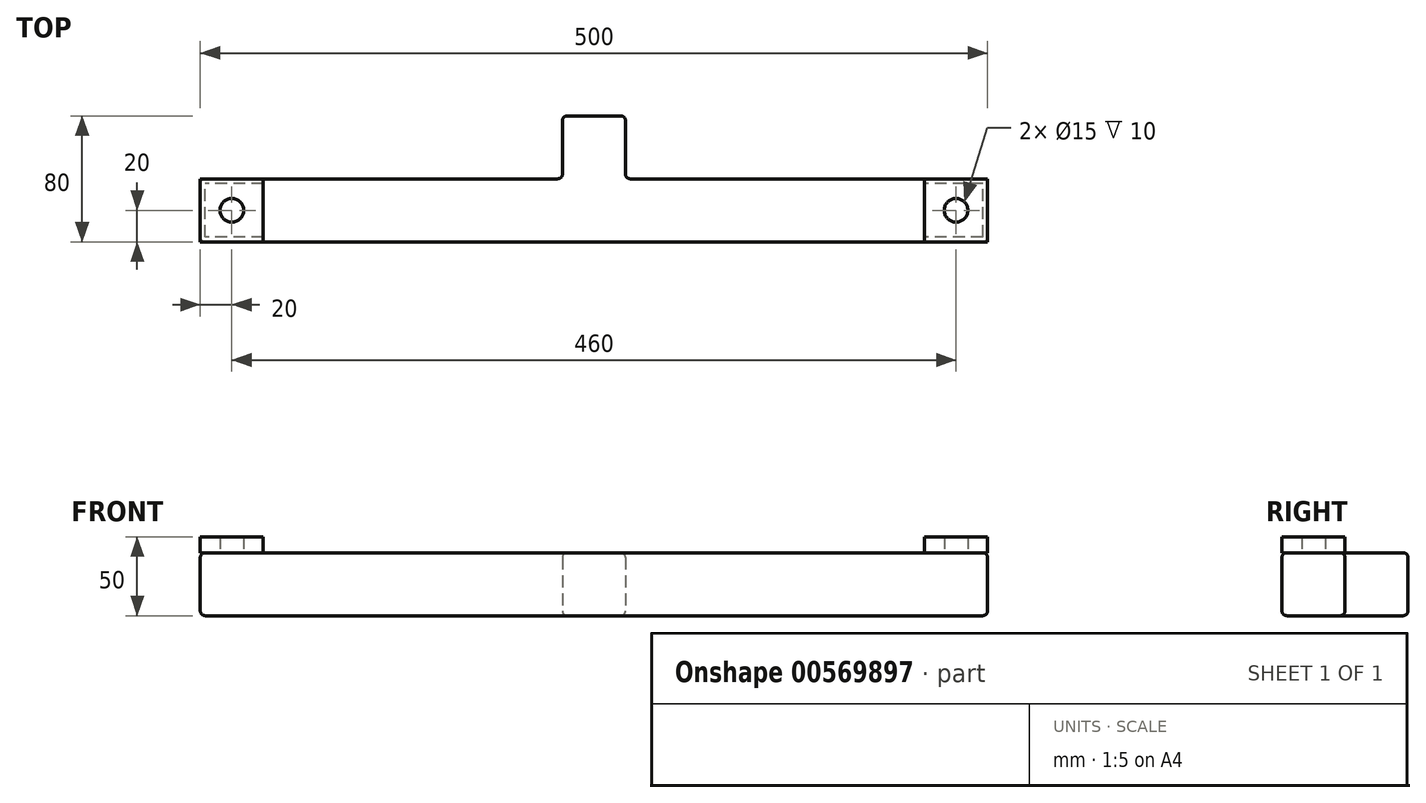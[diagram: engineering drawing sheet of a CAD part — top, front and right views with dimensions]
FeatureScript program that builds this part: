
annotation { "Feature Type Name" : "Feature", "Feature Type Description" : "" }
export const myFeature = defineFeature(function(context is Context, id is Id, definition is map)
    precondition{}
    {
        {
            var Q0;
            Q0=qCreatedBy(makeId("Top.planeOp"),FACE);
            var sketch = newSketch(context, id + "F0", { "sketchPlane" : qUnion([Q0])});
            skLineSegment(sketch, "E0.bottom", {"start": v(250, -20) * mm, "end": v(-250, -20) * mm});
            skLineSegment(sketch, "E0.top", {"start": v(250, 20) * mm, "end": v(20, 20) * mm});
            skLineSegment(sketch, "E0.left", {"start": v(250, -20) * mm, "end": v(250, 20) * mm});
            skLineSegment(sketch, "E0.right", {"start": v(-250, -20) * mm, "end": v(-250, 20) * mm});
            skPoint(sketch, "E0.middle", {"position": v(0, 0) * mm});
            skLineSegment(sketch, "E1.top", {"start": v(-20, 60) * mm, "end": v(20, 60) * mm});
            skLineSegment(sketch, "E1.left", {"start": v(-20, 20) * mm, "end": v(-20, 60) * mm});
            skLineSegment(sketch, "E1.right", {"start": v(20, 20) * mm, "end": v(20, 60) * mm});
            skLineSegment(sketch, "E2.trimOffspring", {"start": v(-20, 20) * mm, "end": v(-250, 20) * mm});
            skSolve(sketch);
        }
        {
            var Q0;
            Q0 = qSketchRegion(id + "F0", true);
            extrude(context, id + "F1", {"entities" : qUnion([Q0]), "depth" : 40 * mm, "offsetDistance" : 25 * mm});
        }
        {
            var Q0;
            Q0=makeQuery(id+"F1.opExtrude","SWEPT_EDGE",EDGE,{"disambiguationData":[OSD([sQuery(id+"F0.wireOp",EDGE,"E0.top"),sQuery(id+"F0.wireOp",EDGE,"E0.left")])]});
            var Q1;
            Q1=makeQuery(id+"F1.opExtrude","SWEPT_EDGE",EDGE,{"disambiguationData":[OSD([sQuery(id+"F0.wireOp",EDGE,"E0.bottom"),sQuery(id+"F0.wireOp",EDGE,"E0.right")])]});
            var Q2;
            Q2=makeQuery(id+"F1.opExtrude","SWEPT_EDGE",EDGE,{"disambiguationData":[OSD([sQuery(id+"F0.wireOp",EDGE,"E0.bottom"),sQuery(id+"F0.wireOp",EDGE,"E0.left")])]});
            var Q3;
            Q3=makeQuery(id+"F1.opExtrude","CAP_EDGE",EDGE,{"disambiguationData":[OSD([sQuery(id+"F0.wireOp",EDGE,"E0.bottom")])],"isStart":true});
            var Q4;
            Q4=makeQuery(id+"F1.opExtrude","CAP_EDGE",EDGE,{"disambiguationData":[OSD([sQuery(id+"F0.wireOp",EDGE,"E0.bottom")])],"isStart":false});
            var Q5;
            Q5=makeQuery(id+"F1.opExtrude","CAP_EDGE",EDGE,{"disambiguationData":[OSD([sQuery(id+"F0.wireOp",EDGE,"E0.top")])],"isStart":false});
            var Q6;
            Q6=makeQuery(id+"F1.opExtrude","CAP_EDGE",EDGE,{"disambiguationData":[OSD([sQuery(id+"F0.wireOp",EDGE,"E0.left")])],"isStart":true});
            var Q7;
            Q7=makeQuery(id+"F1.opExtrude","CAP_EDGE",EDGE,{"disambiguationData":[OSD([sQuery(id+"F0.wireOp",EDGE,"E0.left")])],"isStart":false});
            var Q8;
            Q8=makeQuery(id+"F1.opExtrude","CAP_EDGE",EDGE,{"disambiguationData":[OSD([sQuery(id+"F0.wireOp",EDGE,"E0.right")])],"isStart":false});
            var Q9;
            Q9=makeQuery(id+"F1.opExtrude","SWEPT_EDGE",EDGE,{"disambiguationData":[OSD([sQuery(id+"F0.wireOp",EDGE,"E0.top"),sQuery(id+"F0.wireOp",EDGE,"E1.right")])]});
            var Q10;
            Q10=makeQuery(id+"F1.opExtrude","SWEPT_EDGE",EDGE,{"disambiguationData":[OSD([sQuery(id+"F0.wireOp",EDGE,"E0.right"),sQuery(id+"F0.wireOp",EDGE,"E2.trimOffspring")])]});
            var Q11;
            Q11=makeQuery(id+"F1.opExtrude","CAP_EDGE",EDGE,{"disambiguationData":[OSD([sQuery(id+"F0.wireOp",EDGE,"E0.top")])],"isStart":true});
            var Q12;
            Q12=makeQuery(id+"F1.opExtrude","CAP_EDGE",EDGE,{"disambiguationData":[OSD([sQuery(id+"F0.wireOp",EDGE,"E0.right")])],"isStart":true});
            var Q13;
            Q13=makeQuery(id+"F1.opExtrude","CAP_EDGE",EDGE,{"disambiguationData":[OSD([sQuery(id+"F0.wireOp",EDGE,"E1.right")])],"isStart":true});
            var Q14;
            Q14=makeQuery(id+"F1.opExtrude","CAP_EDGE",EDGE,{"disambiguationData":[OSD([sQuery(id+"F0.wireOp",EDGE,"E1.left")])],"isStart":false});
            var Q15;
            Q15=makeQuery(id+"F1.opExtrude","CAP_EDGE",EDGE,{"disambiguationData":[OSD([sQuery(id+"F0.wireOp",EDGE,"E2.trimOffspring")])],"isStart":false});
            var Q16;
            Q16=makeQuery(id+"F1.opExtrude","CAP_EDGE",EDGE,{"disambiguationData":[OSD([sQuery(id+"F0.wireOp",EDGE,"E1.right")])],"isStart":false});
            var Q17;
            Q17=makeQuery(id+"F1.opExtrude","SWEPT_EDGE",EDGE,{"disambiguationData":[OSD([sQuery(id+"F0.wireOp",EDGE,"E1.top"),sQuery(id+"F0.wireOp",EDGE,"E1.right")])]});
            var Q18;
            Q18=makeQuery(id+"F1.opExtrude","CAP_EDGE",EDGE,{"disambiguationData":[OSD([sQuery(id+"F0.wireOp",EDGE,"E1.top")])],"isStart":false});
            var Q19;
            Q19=makeQuery(id+"F1.opExtrude","CAP_EDGE",EDGE,{"disambiguationData":[OSD([sQuery(id+"F0.wireOp",EDGE,"E2.trimOffspring")])],"isStart":true});
            var Q20;
            Q20=makeQuery(id+"F1.opExtrude","SWEPT_EDGE",EDGE,{"disambiguationData":[OSD([sQuery(id+"F0.wireOp",EDGE,"E1.left"),sQuery(id+"F0.wireOp",EDGE,"E2.trimOffspring")])]});
            var Q21;
            Q21=makeQuery(id+"F1.opExtrude","SWEPT_EDGE",EDGE,{"disambiguationData":[OSD([sQuery(id+"F0.wireOp",EDGE,"E1.top"),sQuery(id+"F0.wireOp",EDGE,"E1.left")])]});
            var Q22;
            Q22=makeQuery(id+"F1.opExtrude","CAP_EDGE",EDGE,{"disambiguationData":[OSD([sQuery(id+"F0.wireOp",EDGE,"E1.left")])],"isStart":true});
            var Q23;
            Q23=makeQuery(id+"F1.opExtrude","CAP_EDGE",EDGE,{"disambiguationData":[OSD([sQuery(id+"F0.wireOp",EDGE,"E1.top")])],"isStart":true});
            fillet(context, id + "F2", {"entities" : qUnion([Q0, Q1, Q2, Q3, Q4, Q5, Q6, Q7, Q8, Q9, Q10, Q11, Q12, Q13, Q14, Q15, Q16, Q17, Q18, Q19, Q20, Q21, Q22, Q23]), "radius" : 3 * mm, "tangentPropagation" : true, "allowEdgeOverflow" : false});
        }
        {
            var Q0;
            Q0=makeQuery(id+"F1.opExtrude","CAP_FACE",FACE,{"disambiguationData":[OSD([sQuery(id+"F0.wireOp",EDGE,"E0.bottom"),sQuery(id+"F0.wireOp",EDGE,"E0.top"),sQuery(id+"F0.wireOp",EDGE,"E0.left"),sQuery(id+"F0.wireOp",EDGE,"E0.right")])],"isStart":false});
            var sketch = newSketch(context, id + "F3", { "sketchPlane" : qUnion([Q0])});
            skLineSegment(sketch, "E3.bottom", {"start": v(-250, 20) * mm, "end": v(-210, 20) * mm});
            skLineSegment(sketch, "E3.top", {"start": v(-250, -20) * mm, "end": v(-210, -20) * mm});
            skLineSegment(sketch, "E3.left", {"start": v(-250, 20) * mm, "end": v(-250, -20) * mm});
            skLineSegment(sketch, "E3.right", {"start": v(-210, 20) * mm, "end": v(-210, -20) * mm});
            skCircle(sketch, "E4", {"center": v(-230, 0) * mm, "radius": 7.5 * mm});
            skLineSegment(sketch, "E5.MirrorCS", {"start": v(250, 20) * mm, "end": v(210, 20) * mm});
            skLineSegment(sketch, "E6.MirrorCS", {"start": v(250, -20) * mm, "end": v(210, -20) * mm});
            skLineSegment(sketch, "E7.MirrorCS", {"start": v(250, 20) * mm, "end": v(250, -20) * mm});
            skCircle(sketch, "E8.MirrorC", {"center": v(230, 0) * mm, "radius": 7.5 * mm});
            skLineSegment(sketch, "E9.MirrorCS", {"start": v(210, 20) * mm, "end": v(210, -20) * mm});
            skSolve(sketch);
        }
        {
            var Q0;
            Q0 = qSketchRegion(id + "F3", true);
            extrude(context, id + "F4", {"entities" : qUnion([Q0]), "operationType" : NewBodyOperationType.ADD, "depth" : 10 * mm, "offsetDistance" : 25 * mm});
        }
    });
